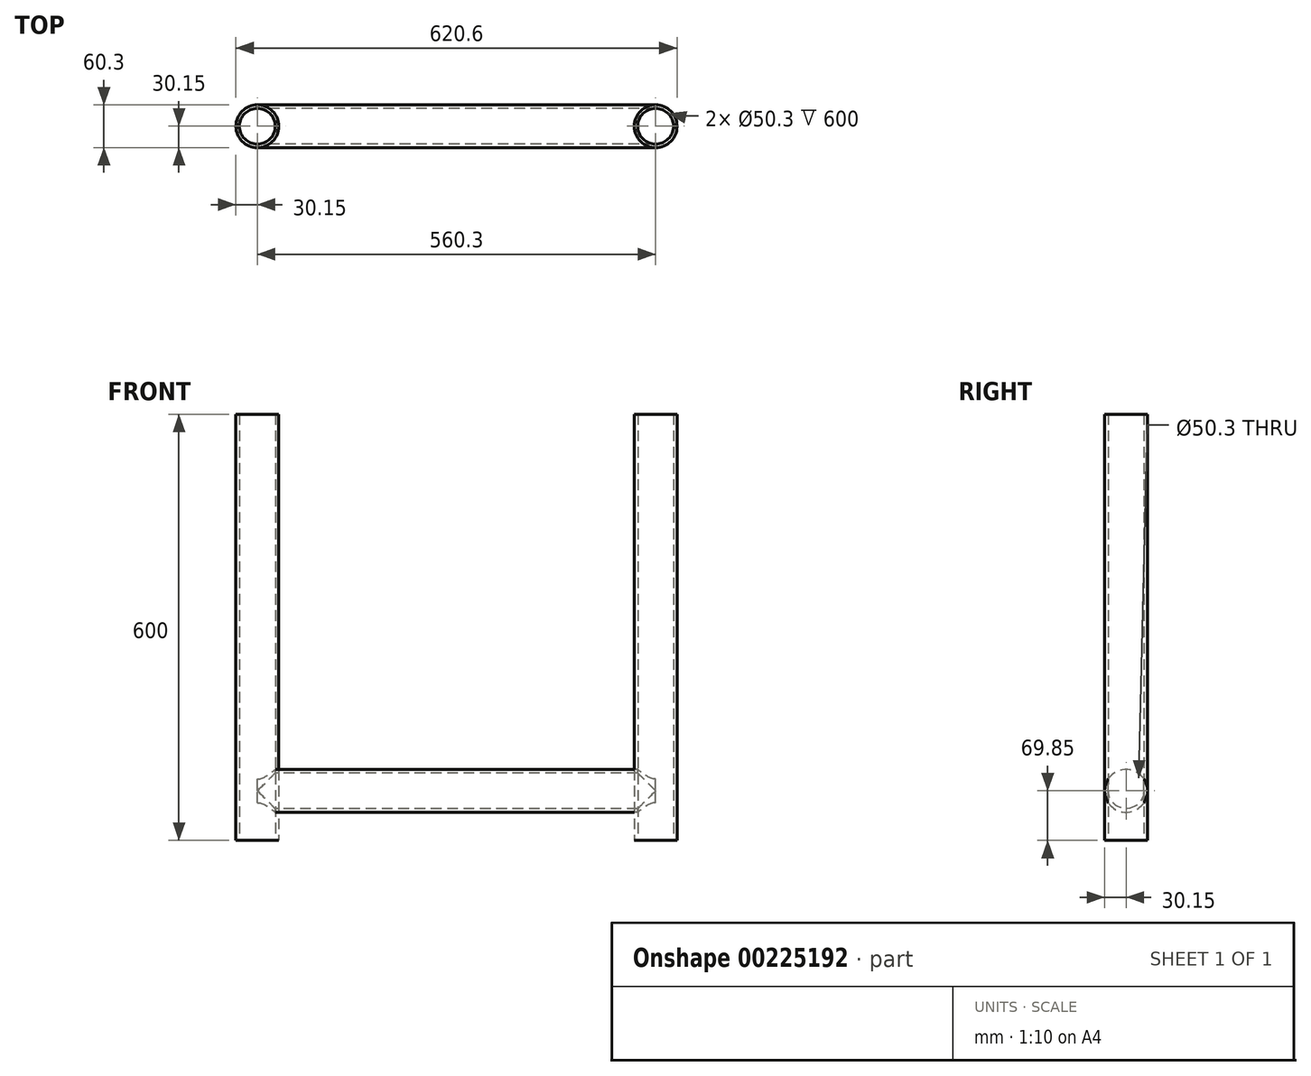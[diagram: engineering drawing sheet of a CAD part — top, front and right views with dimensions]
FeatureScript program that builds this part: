
annotation { "Feature Type Name" : "Feature", "Feature Type Description" : "" }
export const myFeature = defineFeature(function(context is Context, id is Id, definition is map)
    precondition{}
    {
        {
            var Q0;
            Q0=qCreatedBy(makeId("Top.planeOp"),FACE);
            var sketch = newSketch(context, id + "F0", { "sketchPlane" : qUnion([Q0])});
            skCircle(sketch, "E0", {"center": v(0, 0) * mm, "radius": 250 * mm, "construction": true});
            skLineSegment(sketch, "E1", {"start": v(-250, 0) * mm, "end": v(250, 0) * mm, "construction": true});
            skCircle(sketch, "E2", {"center": v(-280.15, 0) * mm, "radius": 30.15 * mm});
            skCircle(sketch, "E3", {"center": v(280.15, 0) * mm, "radius": 30.15 * mm});
            skCircle(sketch, "E4", {"center": v(-280.15, 0) * mm, "radius": 25.15 * mm});
            skCircle(sketch, "E5", {"center": v(280.15, 0) * mm, "radius": 25.15 * mm});
            skSolve(sketch);
        }
        {
            var Q0;
            Q0 = qSketchRegion(id + "F0", true);
            extrude(context, id + "F1", {"entities" : qUnion([Q0]), "depth" : 600 * mm});
        }
        {
            var Q0;
            Q0=qCreatedBy(makeId("Right.planeOp"),FACE);
            var sketch = newSketch(context, id + "F2", { "sketchPlane" : qUnion([Q0])});
            skLineSegment(sketch, "E6", {"start": v(0, 600) * mm, "end": v(0, 0) * mm, "construction": true});
            skCircle(sketch, "E7", {"center": v(0, 69.85) * mm, "radius": 30.15 * mm});
            skCircle(sketch, "E8", {"center": v(0, 69.85) * mm, "radius": 25.15 * mm});
            skSolve(sketch);
        }
        {
            var Q0;
            Q0 = qSketchRegion(id + "F2", true);
            extrude(context, id + "F3", {"entities" : qUnion([Q0]), "depth" : (250 + 60.3 / 2) * mm, "hasSecondDirection" : true, "secondDirectionOppositeDirection" : true, "secondDirectionDepth" : (250 + 60.3 / 2) * mm});
        }
        {
            var Q0;
            Q0=qCreatedBy(makeId("Top.planeOp"),FACE);
            var sketch = newSketch(context, id + "F4", { "sketchPlane" : qUnion([Q0])});
            skCircle(sketch, "E9", {"center": v(-280.15, 0) * mm, "radius": 25.15 * mm});
            skCircle(sketch, "E10", {"center": v(280.15, 0) * mm, "radius": 25.15 * mm});
            skLineSegment(sketch, "E11", {"start": v(255, 0) * mm, "end": v(-255, 0) * mm, "construction": true});
            skSolve(sketch);
        }
        {
            var Q0;
            Q0 = qSketchRegion(id + "F4", true);
            extrude(context, id + "F5", {"entities" : qUnion([Q0]), "operationType" : NewBodyOperationType.REMOVE, "endBound" : BoundingType.THROUGH_ALL, "oppositeDirection" : true, "depth" : 25 * mm, "hasSecondDirection" : true, "secondDirectionBound" : SecondDirectionBoundingType.THROUGH_ALL, "secondDirectionOppositeDirection" : false, "secondDirectionDepth" : 25 * mm});
        }
    });
